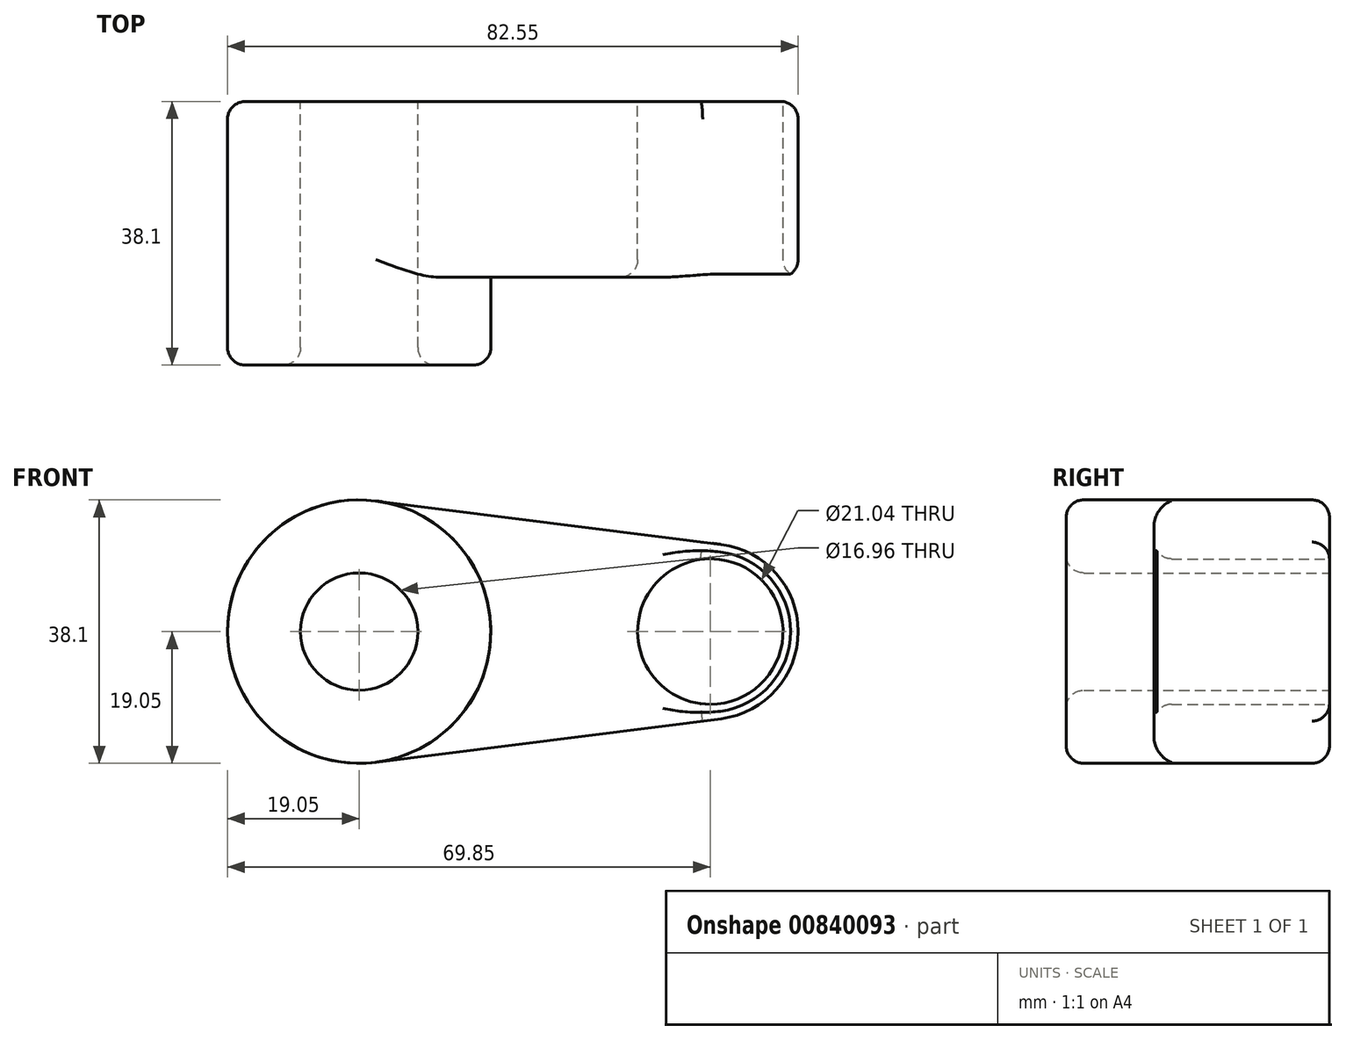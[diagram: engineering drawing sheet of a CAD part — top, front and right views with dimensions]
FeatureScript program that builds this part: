
annotation { "Feature Type Name" : "Feature", "Feature Type Description" : "" }
export const myFeature = defineFeature(function(context is Context, id is Id, definition is map)
    precondition{}
    {
        {
            var Q0;
            Q0=qCreatedBy(makeId("Front.planeOp"),FACE);
            var sketch = newSketch(context, id + "F0", { "sketchPlane" : qUnion([Q0])});
            skCircle(sketch, "E0", {"center": v(0, 0) * mm, "radius": 19.05 * mm});
            skCircle(sketch, "E1", {"center": v(50.8, 0) * mm, "radius": 12.7 * mm});
            skLineSegment(sketch, "E2", {"start": v(2.38, 18.9) * mm, "end": v(52.39, 12.6) * mm});
            skLineSegment(sketch, "E3", {"start": v(2.38, -18.9) * mm, "end": v(52.39, -12.6) * mm});
            skCircle(sketch, "E4", {"center": v(0, 0) * mm, "radius": 8.48 * mm});
            skCircle(sketch, "E5", {"center": v(50.8, 0) * mm, "radius": 10.52 * mm});
            skSolve(sketch);
        }
        {
            var Q0;
            Q0=makeQuery(id+"F0.imprint","IMPRINT",FACE,{"disambiguationData":[TD([[makeQuery(id+"F0.imprint","IMPRINT",EDGE,{"derivedFrom":sQuery(id+"F0.wireOp",EDGE,"E5")}),-1.0]])]});
            var Q1;
            {var subQ0=sQuery(id+"F0.wireOp",EDGE,"E2");Q1=makeQuery(id+"F0.imprint","IMPRINT",FACE,{"disambiguationData":[TD([[makeQuery(id+"F0.imprint","IMPRINT",EDGE,{"derivedFrom":subQ0}),-1.0]])]});}
            var Q2;
            Q2=makeQuery(id+"F0.imprint","IMPRINT",FACE,{"disambiguationData":[TD([[makeQuery(id+"F0.imprint","IMPRINT",EDGE,{"derivedFrom":sQuery(id+"F0.wireOp",EDGE,"E4")}),-1.0]])]});
            extrude(context, id + "F1", {"entities" : qUnion([Q0, Q1, Q2]), "depth" : 25.4 * mm, "offsetDistance" : 25.4 * mm});
        }
        {
            var Q0;
            Q0=makeQuery(id+"F0.imprint","IMPRINT",FACE,{"disambiguationData":[TD([[makeQuery(id+"F0.imprint","IMPRINT",EDGE,{"derivedFrom":sQuery(id+"F0.wireOp",EDGE,"E4")}),-1.0]])]});
            extrude(context, id + "F2", {"entities" : qUnion([Q0]), "operationType" : NewBodyOperationType.ADD, "depth" : 38.1 * mm, "offsetDistance" : 25.4 * mm});
        }
        {
            var Q0;
            Q0=makeQuery(id+"F1.opExtrude","CAP_EDGE",EDGE,{"disambiguationData":[OSD([sQuery(id+"F0.wireOp",EDGE,"E1")])],"isStart":false});
            var Q1;
            Q1=makeQuery(id+"F2.opExtrude","CAP_EDGE",EDGE,{"disambiguationData":[OSD([sQuery(id+"F0.wireOp",EDGE,"E4")])],"isStart":false});
            var Q2;
            Q2=makeQuery(id+"F1.opExtrude","CAP_EDGE",EDGE,{"disambiguationData":[OSD([sQuery(id+"F0.wireOp",EDGE,"E3")])],"isStart":false});
            var Q3;
            Q3=makeQuery(id+"F1.opExtrude","CAP_EDGE",EDGE,{"disambiguationData":[OSD([sQuery(id+"F0.wireOp",EDGE,"E3")])],"isStart":true});
            var Q4;
            Q4=makeQuery(id+"F2.opExtrude","CAP_EDGE",EDGE,{"disambiguationData":[OSD([sQuery(id+"F0.wireOp",EDGE,"E0")])],"isStart":false});
            var Q5;
            Q5=makeQuery(id+"F1.opExtrude","CAP_EDGE",EDGE,{"disambiguationData":[OSD([sQuery(id+"F0.wireOp",EDGE,"E5")])],"isStart":false});
            fillet(context, id + "F3", {"entities" : qUnion([Q0, Q1, Q2, Q3, Q4, Q5]), "radius" : 2.54 * mm, "tangentPropagation" : true, "allowEdgeOverflow" : false});
        }
    });
